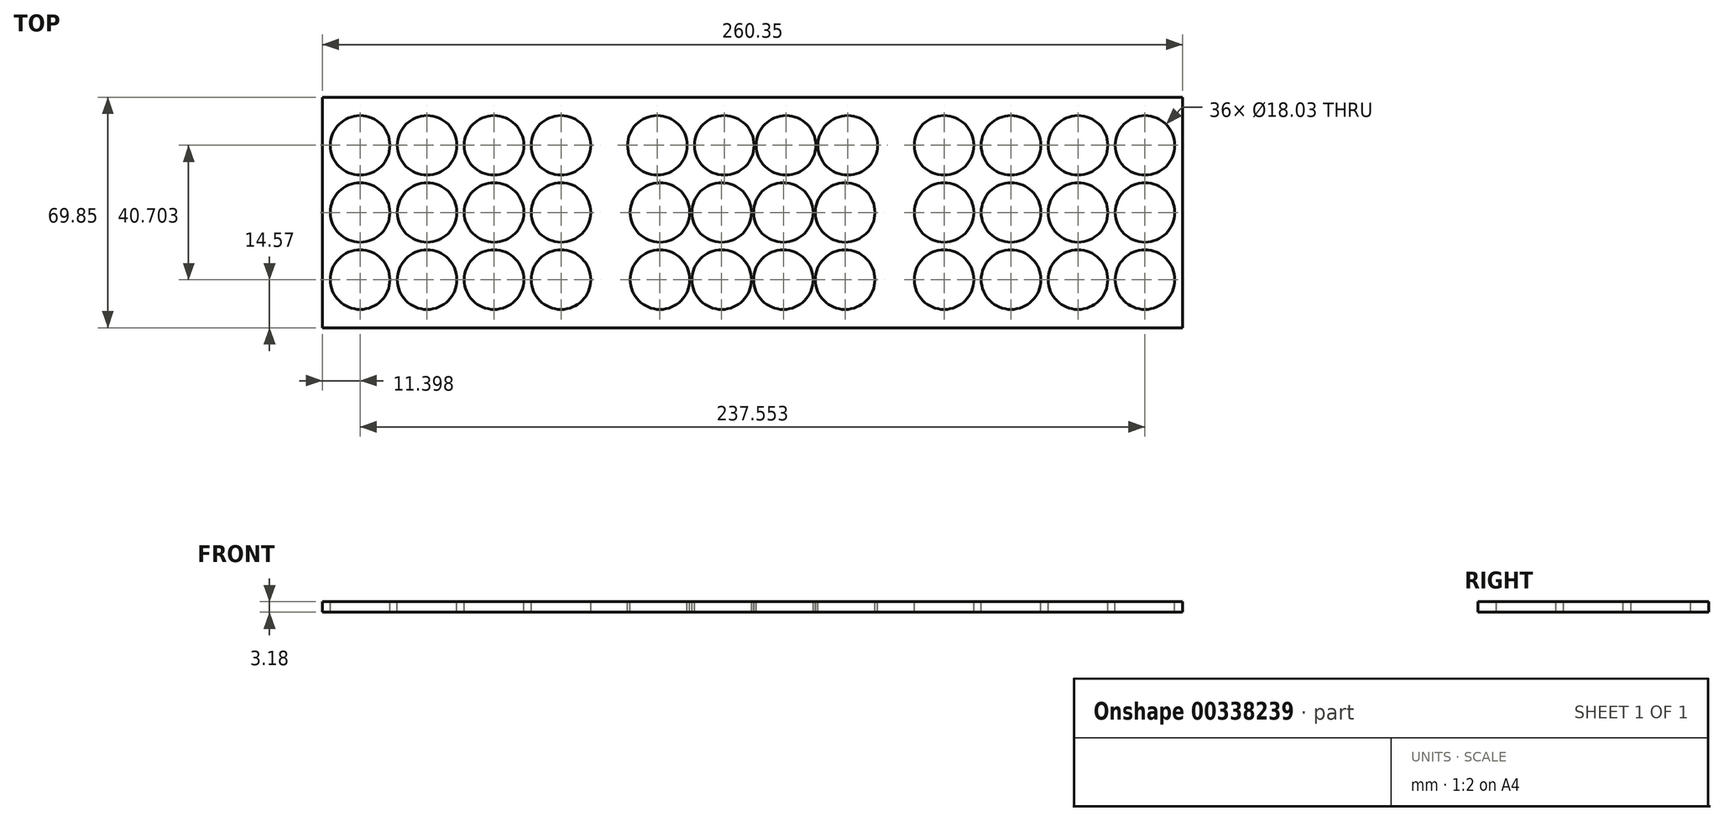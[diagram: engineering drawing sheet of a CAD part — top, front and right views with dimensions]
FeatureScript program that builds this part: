
annotation { "Feature Type Name" : "Feature", "Feature Type Description" : "" }
export const myFeature = defineFeature(function(context is Context, id is Id, definition is map)
    precondition{}
    {
        {
            var Q0;
            Q0=qCreatedBy(makeId("Top.planeOp"),FACE);
            var sketch = newSketch(context, id + "F0", { "sketchPlane" : qUnion([Q0])});
            skLineSegment(sketch, "E0.bottom", {"start": v(0, 0) * mm, "end": v(260.35, 0) * mm});
            skLineSegment(sketch, "E0.top", {"start": v(0, 68.26) * mm, "end": v(260.35, 68.26) * mm});
            skLineSegment(sketch, "E0.left", {"start": v(0, 0) * mm, "end": v(0, 68.26) * mm});
            skLineSegment(sketch, "E0.right", {"start": v(260.35, 0) * mm, "end": v(260.35, 68.26) * mm});
            skSolve(sketch);
        }
        {
            var Q0;
            Q0=qSketchRegion(id+"F0",true);
            extrude(context, id + "F1", {"entities" : qUnion([Q0]), "depth" : 3.17 * mm});
        }
        {
            var Q0;
            Q0=makeQuery(id+"F1.opExtrude","CAP_FACE",FACE,{"disambiguationData":[OSD([sQuery(id+"F0.wireOp",EDGE,"E0.bottom"),sQuery(id+"F0.wireOp",EDGE,"E0.top"),sQuery(id+"F0.wireOp",EDGE,"E0.left"),sQuery(id+"F0.wireOp",EDGE,"E0.right")])],"isStart":false});
            var sketch = newSketch(context, id + "F2", { "sketchPlane" : qUnion([Q0])});
            skLineSegment(sketch, "E1.bottom", {"start": v(0, 0) * mm, "end": v(6.35, 0) * mm});
            skLineSegment(sketch, "E1.top", {"start": v(0, 2.38) * mm, "end": v(6.35, 2.38) * mm});
            skLineSegment(sketch, "E1.left", {"start": v(0, 0) * mm, "end": v(0, 2.38) * mm});
            skLineSegment(sketch, "E1.right", {"start": v(6.35, 0) * mm, "end": v(6.35, 2.38) * mm});
            skLineSegment(sketch, "E2", {"start": v(-2.38, 34.13) * mm, "end": v(0, 34.13) * mm, "construction": true});
            skLineSegment(sketch, "E3.MirrorCS", {"start": v(6.35, 68.26) * mm, "end": v(6.35, 65.88) * mm});
            skLineSegment(sketch, "E4.MirrorCS", {"start": v(0, 65.88) * mm, "end": v(6.35, 65.88) * mm});
            skLineSegment(sketch, "E5.MirrorCS", {"start": v(0, 68.26) * mm, "end": v(6.35, 68.26) * mm});
            skLineSegment(sketch, "E6.MirrorCS", {"start": v(0, 68.26) * mm, "end": v(0, 65.88) * mm});
            skCircle(sketch, "E7", {"center": v(11.4, 54.48) * mm, "radius": 9.02 * mm});
            skLineSegment(sketch, "E8", {"start": v(11.4, 54.48) * mm, "end": v(31.67, 54.48) * mm, "construction": true});
            skCircle(sketch, "E9", {"center": v(31.67, 54.48) * mm, "radius": 9.02 * mm});
            skLineSegment(sketch, "E10.1.0.0", {"start": v(31.67, 54.48) * mm, "end": v(51.94, 54.48) * mm, "construction": true});
            skCircle(sketch, "E10.1.0.1", {"center": v(51.94, 54.48) * mm, "radius": 9.02 * mm});
            skCircle(sketch, "E10.2.0.1", {"center": v(72.21, 54.48) * mm, "radius": 9.02 * mm});
            skLineSegment(sketch, "E11", {"start": v(0, 68.26) * mm, "end": v(0, 155.05) * mm, "construction": true});
            skLineSegment(sketch, "E12", {"start": v(0, 155.05) * mm, "end": v(86.78, 155.05) * mm, "construction": true});
            skLineSegment(sketch, "E13", {"start": v(86.78, 155.05) * mm, "end": v(173.57, 155.05) * mm, "construction": true});
            skLineSegment(sketch, "E14", {"start": v(173.57, 155.05) * mm, "end": v(260.35, 155.05) * mm, "construction": true});
            skLineSegment(sketch, "E15", {"start": v(260.35, 155.05) * mm, "end": v(260.35, 68.26) * mm, "construction": true});
            skLineSegment(sketch, "E16", {"start": v(86.78, 155.05) * mm, "end": v(86.78, 54.48) * mm, "construction": true});
            skLineSegment(sketch, "E17", {"start": v(0, 34.13) * mm, "end": v(2.38, 34.13) * mm, "construction": true});
            skCircle(sketch, "E18", {"center": v(101.36, 54.48) * mm, "radius": 9.02 * mm});
            skLineSegment(sketch, "E19", {"start": v(72.21, 54.48) * mm, "end": v(81.23, 54.48) * mm, "construction": true});
            skLineSegment(sketch, "E20", {"start": v(81.23, 54.48) * mm, "end": v(92.34, 54.48) * mm, "construction": true});
            skLineSegment(sketch, "E21", {"start": v(92.34, 54.48) * mm, "end": v(101.36, 54.48) * mm, "construction": true});
            skLineSegment(sketch, "E22", {"start": v(72.21, 54.48) * mm, "end": v(63.2, 54.48) * mm, "construction": true});
            skLineSegment(sketch, "E23", {"start": v(63.2, 54.48) * mm, "end": v(60.96, 54.48) * mm, "construction": true});
            skLineSegment(sketch, "E24", {"start": v(60.96, 54.48) * mm, "end": v(51.94, 54.48) * mm, "construction": true});
            skLineSegment(sketch, "E25", {"start": v(11.4, 54.48) * mm, "end": v(11.4, 63.5) * mm, "construction": true});
            skLineSegment(sketch, "E26", {"start": v(11.4, 54.48) * mm, "end": v(2.38, 54.48) * mm, "construction": true});
            skLineSegment(sketch, "E27", {"start": v(2.38, 54.48) * mm, "end": v(0, 54.48) * mm, "construction": true});
            skLineSegment(sketch, "E28", {"start": v(51.94, 54.48) * mm, "end": v(51.94, 34.21) * mm, "construction": true});
            skLineSegment(sketch, "E29", {"start": v(51.94, 34.21) * mm, "end": v(72.21, 34.21) * mm, "construction": true});
            skLineSegment(sketch, "E30", {"start": v(72.21, 34.21) * mm, "end": v(72.21, 54.48) * mm, "construction": true});
            skLineSegment(sketch, "E31", {"start": v(2.38, 34.13) * mm, "end": v(11.4, 34.13) * mm, "construction": true});
            skLineSegment(sketch, "E32", {"start": v(173.57, 155.05) * mm, "end": v(173.57, 54.48) * mm});
            skLineSegment(sketch, "E33", {"start": v(168.01, 54.48) * mm, "end": v(179.12, 54.48) * mm, "construction": true});
            skLineSegment(sketch, "E34", {"start": v(101.36, 54.48) * mm, "end": v(121.63, 54.48) * mm, "construction": true});
            skCircle(sketch, "E35", {"center": v(121.63, 54.48) * mm, "radius": 9.02 * mm});
            skCircle(sketch, "E36.1.0.0", {"center": v(140.31, 54.48) * mm, "radius": 9.02 * mm});
            skLineSegment(sketch, "E36.1.0.1", {"start": v(121.63, 54.48) * mm, "end": v(140.31, 54.48) * mm, "construction": true});
            skCircle(sketch, "E36.2.0.0", {"center": v(159, 54.48) * mm, "radius": 9.02 * mm});
            skLineSegment(sketch, "E36.2.0.1", {"start": v(140.31, 54.48) * mm, "end": v(159, 54.48) * mm, "construction": true});
            skLineSegment(sketch, "E37", {"start": v(159, 54.48) * mm, "end": v(168.01, 54.48) * mm, "construction": true});
            skLineSegment(sketch, "E38", {"start": v(179.12, 54.48) * mm, "end": v(188.14, 54.48) * mm, "construction": true});
            skCircle(sketch, "E39", {"center": v(188.14, 54.48) * mm, "radius": 9.02 * mm});
            skLineSegment(sketch, "E40", {"start": v(188.14, 54.48) * mm, "end": v(208.41, 54.48) * mm, "construction": true});
            skLineSegment(sketch, "E41", {"start": v(208.41, 54.48) * mm, "end": v(228.68, 54.48) * mm, "construction": true});
            skLineSegment(sketch, "E42", {"start": v(228.68, 54.48) * mm, "end": v(248.95, 54.48) * mm, "construction": true});
            skCircle(sketch, "E43", {"center": v(208.41, 54.48) * mm, "radius": 9.02 * mm});
            skCircle(sketch, "E44", {"center": v(228.68, 54.48) * mm, "radius": 9.02 * mm});
            skCircle(sketch, "E45", {"center": v(248.95, 54.48) * mm, "radius": 9.02 * mm});
            skCircle(sketch, "E46", {"center": v(11.4, 34.13) * mm, "radius": 9.02 * mm});
            skLineSegment(sketch, "E47", {"start": v(11.4, 34.13) * mm, "end": v(31.67, 34.13) * mm, "construction": true});
            skLineSegment(sketch, "E48", {"start": v(31.67, 34.13) * mm, "end": v(51.94, 34.13) * mm, "construction": true});
            skLineSegment(sketch, "E49", {"start": v(51.94, 34.13) * mm, "end": v(72.21, 34.13) * mm, "construction": true});
            skCircle(sketch, "E50", {"center": v(31.67, 34.13) * mm, "radius": 9.02 * mm});
            skCircle(sketch, "E51", {"center": v(51.94, 34.13) * mm, "radius": 9.02 * mm});
            skCircle(sketch, "E52", {"center": v(72.21, 34.13) * mm, "radius": 9.02 * mm});
            skLineSegment(sketch, "E53", {"start": v(260.35, 34.13) * mm, "end": v(257.97, 34.13) * mm, "construction": true});
            skLineSegment(sketch, "E54", {"start": v(257.97, 34.13) * mm, "end": v(248.95, 34.13) * mm, "construction": true});
            skCircle(sketch, "E55", {"center": v(248.95, 34.13) * mm, "radius": 9.02 * mm});
            skLineSegment(sketch, "E56", {"start": v(248.95, 34.13) * mm, "end": v(228.68, 34.13) * mm, "construction": true});
            skLineSegment(sketch, "E57", {"start": v(228.68, 34.13) * mm, "end": v(208.41, 34.13) * mm, "construction": true});
            skLineSegment(sketch, "E58", {"start": v(208.41, 34.13) * mm, "end": v(188.14, 34.13) * mm, "construction": true});
            skCircle(sketch, "E59", {"center": v(228.68, 34.13) * mm, "radius": 9.02 * mm});
            skCircle(sketch, "E60", {"center": v(208.41, 34.13) * mm, "radius": 9.02 * mm});
            skCircle(sketch, "E61", {"center": v(188.14, 34.13) * mm, "radius": 9.02 * mm});
            skLineSegment(sketch, "E62", {"start": v(72.21, 34.13) * mm, "end": v(102.15, 34.13) * mm, "construction": true});
            skLineSegment(sketch, "E63", {"start": v(102.15, 34.13) * mm, "end": v(120.83, 34.13) * mm, "construction": true});
            skLineSegment(sketch, "E64", {"start": v(120.83, 34.13) * mm, "end": v(139.52, 34.13) * mm, "construction": true});
            skLineSegment(sketch, "E65", {"start": v(139.52, 34.13) * mm, "end": v(158.2, 34.13) * mm, "construction": true});
            skCircle(sketch, "E66", {"center": v(102.15, 34.13) * mm, "radius": 9.02 * mm});
            skCircle(sketch, "E67", {"center": v(120.83, 34.13) * mm, "radius": 9.02 * mm});
            skCircle(sketch, "E68", {"center": v(139.52, 34.13) * mm, "radius": 9.02 * mm});
            skCircle(sketch, "E69", {"center": v(158.2, 34.13) * mm, "radius": 9.02 * mm});
            skLineSegment(sketch, "E70", {"start": v(158.2, 34.13) * mm, "end": v(188.14, 34.13) * mm, "construction": true});
            skLineSegment(sketch, "E71", {"start": v(0, 13.78) * mm, "end": v(2.38, 13.78) * mm, "construction": true});
            skLineSegment(sketch, "E72", {"start": v(2.38, 13.78) * mm, "end": v(11.4, 13.78) * mm, "construction": true});
            skCircle(sketch, "E73", {"center": v(11.4, 13.78) * mm, "radius": 9.02 * mm});
            skLineSegment(sketch, "E74", {"start": v(11.4, 13.78) * mm, "end": v(11.4, 4.76) * mm, "construction": true});
            skLineSegment(sketch, "E75", {"start": v(11.4, 4.76) * mm, "end": v(11.4, 2.38) * mm, "construction": true});
            skLineSegment(sketch, "E76", {"start": v(260.35, 13.78) * mm, "end": v(257.97, 13.78) * mm, "construction": true});
            skLineSegment(sketch, "E77", {"start": v(257.97, 13.78) * mm, "end": v(248.95, 13.78) * mm, "construction": true});
            skLineSegment(sketch, "E78", {"start": v(248.95, 13.78) * mm, "end": v(248.95, 4.76) * mm, "construction": true});
            skLineSegment(sketch, "E79", {"start": v(248.95, 4.76) * mm, "end": v(248.95, 2.38) * mm, "construction": true});
            skCircle(sketch, "E80", {"center": v(248.95, 13.78) * mm, "radius": 9.02 * mm});
            skLineSegment(sketch, "E81", {"start": v(248.95, 13.78) * mm, "end": v(228.68, 13.78) * mm, "construction": true});
            skLineSegment(sketch, "E82", {"start": v(228.68, 13.78) * mm, "end": v(208.41, 13.78) * mm, "construction": true});
            skLineSegment(sketch, "E83", {"start": v(208.41, 13.78) * mm, "end": v(188.14, 13.78) * mm, "construction": true});
            skCircle(sketch, "E84", {"center": v(228.68, 13.78) * mm, "radius": 9.02 * mm});
            skCircle(sketch, "E85", {"center": v(208.41, 13.78) * mm, "radius": 9.02 * mm});
            skCircle(sketch, "E86", {"center": v(188.14, 13.78) * mm, "radius": 9.02 * mm});
            skLineSegment(sketch, "E87", {"start": v(11.4, 13.78) * mm, "end": v(31.67, 13.78) * mm, "construction": true});
            skLineSegment(sketch, "E88", {"start": v(31.67, 13.78) * mm, "end": v(51.94, 13.78) * mm, "construction": true});
            skLineSegment(sketch, "E89", {"start": v(51.94, 13.78) * mm, "end": v(72.21, 13.78) * mm, "construction": true});
            skCircle(sketch, "E90", {"center": v(31.67, 13.78) * mm, "radius": 9.02 * mm});
            skCircle(sketch, "E91", {"center": v(51.94, 13.78) * mm, "radius": 9.02 * mm});
            skCircle(sketch, "E92", {"center": v(72.21, 13.78) * mm, "radius": 9.02 * mm});
            skLineSegment(sketch, "E93", {"start": v(102.15, 13.78) * mm, "end": v(120.83, 13.78) * mm, "construction": true});
            skLineSegment(sketch, "E94", {"start": v(120.83, 13.78) * mm, "end": v(139.52, 13.78) * mm, "construction": true});
            skLineSegment(sketch, "E95", {"start": v(139.52, 13.78) * mm, "end": v(158.2, 13.78) * mm, "construction": true});
            skCircle(sketch, "E96", {"center": v(102.15, 13.78) * mm, "radius": 9.02 * mm});
            skCircle(sketch, "E97", {"center": v(120.83, 13.78) * mm, "radius": 9.02 * mm});
            skCircle(sketch, "E98", {"center": v(139.52, 13.78) * mm, "radius": 9.02 * mm});
            skCircle(sketch, "E99", {"center": v(158.2, 13.78) * mm, "radius": 9.02 * mm});
            skLineSegment(sketch, "E100", {"start": v(72.21, 13.78) * mm, "end": v(102.15, 13.78) * mm, "construction": true});
            skLineSegment(sketch, "E101", {"start": v(188.14, 13.78) * mm, "end": v(158.2, 13.78) * mm, "construction": true});
            skLineSegment(sketch, "E102", {"start": v(6.35, 65.88) * mm, "end": v(12.7, 65.88) * mm, "construction": true});
            skLineSegment(sketch, "E103.bottom", {"start": v(12.7, 65.88) * mm, "end": v(19.05, 65.88) * mm});
            skLineSegment(sketch, "E103.top", {"start": v(12.7, 68.26) * mm, "end": v(19.05, 68.26) * mm});
            skLineSegment(sketch, "E103.left", {"start": v(12.7, 65.88) * mm, "end": v(12.7, 68.26) * mm});
            skLineSegment(sketch, "E103.right", {"start": v(19.05, 65.88) * mm, "end": v(19.05, 68.26) * mm});
            skLineSegment(sketch, "E104", {"start": v(6.35, 2.38) * mm, "end": v(12.7, 2.38) * mm, "construction": true});
            skLineSegment(sketch, "E105.bottom", {"start": v(12.7, 2.38) * mm, "end": v(19.05, 2.38) * mm});
            skLineSegment(sketch, "E105.top", {"start": v(12.7, 0) * mm, "end": v(19.05, 0) * mm});
            skLineSegment(sketch, "E105.left", {"start": v(12.7, 2.38) * mm, "end": v(12.7, 0) * mm});
            skLineSegment(sketch, "E105.right", {"start": v(19.05, 2.38) * mm, "end": v(19.05, 0) * mm});
            skLineSegment(sketch, "E106.1.0.0", {"start": v(25.4, 2.38) * mm, "end": v(31.75, 2.38) * mm});
            skLineSegment(sketch, "E106.1.0.1", {"start": v(25.4, 0) * mm, "end": v(31.75, 0) * mm});
            skLineSegment(sketch, "E106.1.0.2", {"start": v(19.05, 2.38) * mm, "end": v(25.4, 2.38) * mm, "construction": true});
            skLineSegment(sketch, "E106.1.0.3", {"start": v(25.4, 2.38) * mm, "end": v(25.4, 0) * mm});
            skLineSegment(sketch, "E106.1.0.4", {"start": v(31.75, 2.38) * mm, "end": v(31.75, 0) * mm});
            skLineSegment(sketch, "E106.2.0.0", {"start": v(38.1, 2.38) * mm, "end": v(44.45, 2.38) * mm});
            skLineSegment(sketch, "E106.2.0.1", {"start": v(38.1, 0) * mm, "end": v(44.45, 0) * mm});
            skLineSegment(sketch, "E106.2.0.2", {"start": v(31.75, 2.38) * mm, "end": v(38.1, 2.38) * mm, "construction": true});
            skLineSegment(sketch, "E106.2.0.3", {"start": v(38.1, 2.38) * mm, "end": v(38.1, 0) * mm});
            skLineSegment(sketch, "E106.2.0.4", {"start": v(44.45, 2.38) * mm, "end": v(44.45, 0) * mm});
            skLineSegment(sketch, "E106.direction1", {"start": v(6.35, 2.38) * mm, "end": v(19.05, 2.38) * mm, "construction": true});
            skLineSegment(sketch, "E107.0.3.0", {"start": v(50.8, 2.38) * mm, "end": v(57.15, 2.38) * mm});
            skLineSegment(sketch, "E107.3.3.0", {"start": v(50.8, 0) * mm, "end": v(57.15, 0) * mm});
            skLineSegment(sketch, "E107.6.3.0", {"start": v(44.45, 2.38) * mm, "end": v(50.8, 2.38) * mm, "construction": true});
            skLineSegment(sketch, "E107.9.3.0", {"start": v(50.8, 2.38) * mm, "end": v(50.8, 0) * mm});
            skLineSegment(sketch, "E107.12.3.0", {"start": v(57.15, 2.38) * mm, "end": v(57.15, 0) * mm});
            skLineSegment(sketch, "E107.0.4.0", {"start": v(63.5, 2.38) * mm, "end": v(69.85, 2.38) * mm});
            skLineSegment(sketch, "E107.3.4.0", {"start": v(63.5, 0) * mm, "end": v(69.85, 0) * mm});
            skLineSegment(sketch, "E107.6.4.0", {"start": v(57.15, 2.38) * mm, "end": v(63.5, 2.38) * mm, "construction": true});
            skLineSegment(sketch, "E107.9.4.0", {"start": v(63.5, 2.38) * mm, "end": v(63.5, 0) * mm});
            skLineSegment(sketch, "E107.12.4.0", {"start": v(69.85, 2.38) * mm, "end": v(69.85, 0) * mm});
            skLineSegment(sketch, "E107.0.5.0", {"start": v(76.2, 2.38) * mm, "end": v(82.55, 2.38) * mm});
            skLineSegment(sketch, "E107.3.5.0", {"start": v(76.2, 0) * mm, "end": v(82.55, 0) * mm});
            skLineSegment(sketch, "E107.6.5.0", {"start": v(69.85, 2.38) * mm, "end": v(76.2, 2.38) * mm, "construction": true});
            skLineSegment(sketch, "E107.9.5.0", {"start": v(76.2, 2.38) * mm, "end": v(76.2, 0) * mm});
            skLineSegment(sketch, "E107.12.5.0", {"start": v(82.55, 2.38) * mm, "end": v(82.55, 0) * mm});
            skLineSegment(sketch, "E107.0.6.0", {"start": v(88.9, 2.38) * mm, "end": v(95.25, 2.38) * mm});
            skLineSegment(sketch, "E107.3.6.0", {"start": v(88.9, 0) * mm, "end": v(95.25, 0) * mm});
            skLineSegment(sketch, "E107.6.6.0", {"start": v(82.55, 2.38) * mm, "end": v(88.9, 2.38) * mm, "construction": true});
            skLineSegment(sketch, "E107.9.6.0", {"start": v(88.9, 2.38) * mm, "end": v(88.9, 0) * mm});
            skLineSegment(sketch, "E107.12.6.0", {"start": v(95.25, 2.38) * mm, "end": v(95.25, 0) * mm});
            skLineSegment(sketch, "E107.0.7.0", {"start": v(101.6, 2.38) * mm, "end": v(107.95, 2.38) * mm});
            skLineSegment(sketch, "E107.3.7.0", {"start": v(101.6, 0) * mm, "end": v(107.95, 0) * mm});
            skLineSegment(sketch, "E107.6.7.0", {"start": v(95.25, 2.38) * mm, "end": v(101.6, 2.38) * mm, "construction": true});
            skLineSegment(sketch, "E107.9.7.0", {"start": v(101.6, 2.38) * mm, "end": v(101.6, 0) * mm});
            skLineSegment(sketch, "E107.12.7.0", {"start": v(107.95, 2.38) * mm, "end": v(107.95, 0) * mm});
            skLineSegment(sketch, "E107.0.8.0", {"start": v(114.3, 2.38) * mm, "end": v(120.65, 2.38) * mm});
            skLineSegment(sketch, "E107.3.8.0", {"start": v(114.3, 0) * mm, "end": v(120.65, 0) * mm});
            skLineSegment(sketch, "E107.6.8.0", {"start": v(107.95, 2.38) * mm, "end": v(114.3, 2.38) * mm, "construction": true});
            skLineSegment(sketch, "E107.9.8.0", {"start": v(114.3, 2.38) * mm, "end": v(114.3, 0) * mm});
            skLineSegment(sketch, "E107.12.8.0", {"start": v(120.65, 2.38) * mm, "end": v(120.65, 0) * mm});
            skLineSegment(sketch, "E107.0.9.0", {"start": v(127, 2.38) * mm, "end": v(133.35, 2.38) * mm});
            skLineSegment(sketch, "E107.3.9.0", {"start": v(127, 0) * mm, "end": v(133.35, 0) * mm});
            skLineSegment(sketch, "E107.6.9.0", {"start": v(120.65, 2.38) * mm, "end": v(127, 2.38) * mm, "construction": true});
            skLineSegment(sketch, "E107.9.9.0", {"start": v(127, 2.38) * mm, "end": v(127, 0) * mm});
            skLineSegment(sketch, "E107.12.9.0", {"start": v(133.35, 2.38) * mm, "end": v(133.35, 0) * mm});
            skLineSegment(sketch, "E107.0.10.0", {"start": v(139.7, 2.38) * mm, "end": v(146.05, 2.38) * mm});
            skLineSegment(sketch, "E107.3.10.0", {"start": v(139.7, 0) * mm, "end": v(146.05, 0) * mm});
            skLineSegment(sketch, "E107.6.10.0", {"start": v(133.35, 2.38) * mm, "end": v(139.7, 2.38) * mm, "construction": true});
            skLineSegment(sketch, "E107.9.10.0", {"start": v(139.7, 2.38) * mm, "end": v(139.7, 0) * mm});
            skLineSegment(sketch, "E107.12.10.0", {"start": v(146.05, 2.38) * mm, "end": v(146.05, 0) * mm});
            skLineSegment(sketch, "E107.0.11.0", {"start": v(152.4, 2.38) * mm, "end": v(158.75, 2.38) * mm});
            skLineSegment(sketch, "E107.3.11.0", {"start": v(152.4, 0) * mm, "end": v(158.75, 0) * mm});
            skLineSegment(sketch, "E107.6.11.0", {"start": v(146.05, 2.38) * mm, "end": v(152.4, 2.38) * mm, "construction": true});
            skLineSegment(sketch, "E107.9.11.0", {"start": v(152.4, 2.38) * mm, "end": v(152.4, 0) * mm});
            skLineSegment(sketch, "E107.12.11.0", {"start": v(158.75, 2.38) * mm, "end": v(158.75, 0) * mm});
            skLineSegment(sketch, "E107.0.12.0", {"start": v(165.1, 2.38) * mm, "end": v(171.45, 2.38) * mm});
            skLineSegment(sketch, "E107.3.12.0", {"start": v(165.1, 0) * mm, "end": v(171.45, 0) * mm});
            skLineSegment(sketch, "E107.6.12.0", {"start": v(158.75, 2.38) * mm, "end": v(165.1, 2.38) * mm, "construction": true});
            skLineSegment(sketch, "E107.9.12.0", {"start": v(165.1, 2.38) * mm, "end": v(165.1, 0) * mm});
            skLineSegment(sketch, "E107.12.12.0", {"start": v(171.45, 2.38) * mm, "end": v(171.45, 0) * mm});
            skLineSegment(sketch, "E107.0.13.0", {"start": v(177.8, 2.38) * mm, "end": v(184.15, 2.38) * mm});
            skLineSegment(sketch, "E107.3.13.0", {"start": v(177.8, 0) * mm, "end": v(184.15, 0) * mm});
            skLineSegment(sketch, "E107.6.13.0", {"start": v(171.45, 2.38) * mm, "end": v(177.8, 2.38) * mm, "construction": true});
            skLineSegment(sketch, "E107.9.13.0", {"start": v(177.8, 2.38) * mm, "end": v(177.8, 0) * mm});
            skLineSegment(sketch, "E107.12.13.0", {"start": v(184.15, 2.38) * mm, "end": v(184.15, 0) * mm});
            skLineSegment(sketch, "E107.0.14.0", {"start": v(190.5, 2.38) * mm, "end": v(196.85, 2.38) * mm});
            skLineSegment(sketch, "E107.3.14.0", {"start": v(190.5, 0) * mm, "end": v(196.85, 0) * mm});
            skLineSegment(sketch, "E107.6.14.0", {"start": v(184.15, 2.38) * mm, "end": v(190.5, 2.38) * mm, "construction": true});
            skLineSegment(sketch, "E107.9.14.0", {"start": v(190.5, 2.38) * mm, "end": v(190.5, 0) * mm});
            skLineSegment(sketch, "E107.12.14.0", {"start": v(196.85, 2.38) * mm, "end": v(196.85, 0) * mm});
            skLineSegment(sketch, "E107.0.15.0", {"start": v(203.2, 2.38) * mm, "end": v(209.55, 2.38) * mm});
            skLineSegment(sketch, "E107.3.15.0", {"start": v(203.2, 0) * mm, "end": v(209.55, 0) * mm});
            skLineSegment(sketch, "E107.6.15.0", {"start": v(196.85, 2.38) * mm, "end": v(203.2, 2.38) * mm, "construction": true});
            skLineSegment(sketch, "E107.9.15.0", {"start": v(203.2, 2.38) * mm, "end": v(203.2, 0) * mm});
            skLineSegment(sketch, "E107.12.15.0", {"start": v(209.55, 2.38) * mm, "end": v(209.55, 0) * mm});
            skLineSegment(sketch, "E107.0.16.0", {"start": v(215.9, 2.38) * mm, "end": v(222.25, 2.38) * mm});
            skLineSegment(sketch, "E107.3.16.0", {"start": v(215.9, 0) * mm, "end": v(222.25, 0) * mm});
            skLineSegment(sketch, "E107.6.16.0", {"start": v(209.55, 2.38) * mm, "end": v(215.9, 2.38) * mm, "construction": true});
            skLineSegment(sketch, "E107.9.16.0", {"start": v(215.9, 2.38) * mm, "end": v(215.9, 0) * mm});
            skLineSegment(sketch, "E107.12.16.0", {"start": v(222.25, 2.38) * mm, "end": v(222.25, 0) * mm});
            skLineSegment(sketch, "E107.0.17.0", {"start": v(228.6, 2.38) * mm, "end": v(234.95, 2.38) * mm});
            skLineSegment(sketch, "E107.3.17.0", {"start": v(228.6, 0) * mm, "end": v(234.95, 0) * mm});
            skLineSegment(sketch, "E107.6.17.0", {"start": v(222.25, 2.38) * mm, "end": v(228.6, 2.38) * mm, "construction": true});
            skLineSegment(sketch, "E107.9.17.0", {"start": v(228.6, 2.38) * mm, "end": v(228.6, 0) * mm});
            skLineSegment(sketch, "E107.12.17.0", {"start": v(234.95, 2.38) * mm, "end": v(234.95, 0) * mm});
            skLineSegment(sketch, "E107.0.18.0", {"start": v(241.3, 2.38) * mm, "end": v(247.65, 2.38) * mm});
            skLineSegment(sketch, "E107.3.18.0", {"start": v(241.3, 0) * mm, "end": v(247.65, 0) * mm});
            skLineSegment(sketch, "E107.6.18.0", {"start": v(234.95, 2.38) * mm, "end": v(241.3, 2.38) * mm, "construction": true});
            skLineSegment(sketch, "E107.9.18.0", {"start": v(241.3, 2.38) * mm, "end": v(241.3, 0) * mm});
            skLineSegment(sketch, "E107.12.18.0", {"start": v(247.65, 2.38) * mm, "end": v(247.65, 0) * mm});
            skLineSegment(sketch, "E107.0.19.0", {"start": v(254, 2.38) * mm, "end": v(260.35, 2.38) * mm});
            skLineSegment(sketch, "E107.3.19.0", {"start": v(254, 0) * mm, "end": v(260.35, 0) * mm});
            skLineSegment(sketch, "E107.6.19.0", {"start": v(247.65, 2.38) * mm, "end": v(254, 2.38) * mm, "construction": true});
            skLineSegment(sketch, "E107.9.19.0", {"start": v(254, 2.38) * mm, "end": v(254, 0) * mm});
            skLineSegment(sketch, "E107.12.19.0", {"start": v(260.35, 2.38) * mm, "end": v(260.35, 0) * mm});
            skLineSegment(sketch, "E107.0.20.0", {"start": v(266.7, 2.38) * mm, "end": v(273.05, 2.38) * mm});
            skLineSegment(sketch, "E107.3.20.0", {"start": v(266.7, 0) * mm, "end": v(273.05, 0) * mm});
            skLineSegment(sketch, "E107.6.20.0", {"start": v(260.35, 2.38) * mm, "end": v(266.7, 2.38) * mm, "construction": true});
            skLineSegment(sketch, "E107.9.20.0", {"start": v(266.7, 2.38) * mm, "end": v(266.7, 0) * mm});
            skLineSegment(sketch, "E107.12.20.0", {"start": v(273.05, 2.38) * mm, "end": v(273.05, 0) * mm});
            skLineSegment(sketch, "E107.0.21.0", {"start": v(279.4, 2.38) * mm, "end": v(285.75, 2.38) * mm});
            skLineSegment(sketch, "E107.3.21.0", {"start": v(279.4, 0) * mm, "end": v(285.75, 0) * mm});
            skLineSegment(sketch, "E107.6.21.0", {"start": v(273.05, 2.38) * mm, "end": v(279.4, 2.38) * mm, "construction": true});
            skLineSegment(sketch, "E107.9.21.0", {"start": v(279.4, 2.38) * mm, "end": v(279.4, 0) * mm});
            skLineSegment(sketch, "E107.12.21.0", {"start": v(285.75, 2.38) * mm, "end": v(285.75, 0) * mm});
            skLineSegment(sketch, "E108.1.0.0", {"start": v(25.4, 65.88) * mm, "end": v(31.75, 65.88) * mm});
            skLineSegment(sketch, "E108.1.0.1", {"start": v(25.4, 65.88) * mm, "end": v(25.4, 68.26) * mm});
            skLineSegment(sketch, "E108.1.0.2", {"start": v(25.4, 68.26) * mm, "end": v(31.75, 68.26) * mm});
            skLineSegment(sketch, "E108.1.0.3", {"start": v(31.75, 65.88) * mm, "end": v(31.75, 68.26) * mm});
            skLineSegment(sketch, "E108.1.0.4", {"start": v(19.05, 65.88) * mm, "end": v(25.4, 65.88) * mm, "construction": true});
            skLineSegment(sketch, "E108.2.0.0", {"start": v(38.1, 65.88) * mm, "end": v(44.45, 65.88) * mm});
            skLineSegment(sketch, "E108.2.0.1", {"start": v(38.1, 65.88) * mm, "end": v(38.1, 68.26) * mm});
            skLineSegment(sketch, "E108.2.0.2", {"start": v(38.1, 68.26) * mm, "end": v(44.45, 68.26) * mm});
            skLineSegment(sketch, "E108.2.0.3", {"start": v(44.45, 65.88) * mm, "end": v(44.45, 68.26) * mm});
            skLineSegment(sketch, "E108.2.0.4", {"start": v(31.75, 65.88) * mm, "end": v(38.1, 65.88) * mm, "construction": true});
            skLineSegment(sketch, "E108.3.0.0", {"start": v(50.8, 65.88) * mm, "end": v(57.15, 65.88) * mm});
            skLineSegment(sketch, "E108.3.0.1", {"start": v(50.8, 65.88) * mm, "end": v(50.8, 68.26) * mm});
            skLineSegment(sketch, "E108.3.0.2", {"start": v(50.8, 68.26) * mm, "end": v(57.15, 68.26) * mm});
            skLineSegment(sketch, "E108.3.0.3", {"start": v(57.15, 65.88) * mm, "end": v(57.15, 68.26) * mm});
            skLineSegment(sketch, "E108.3.0.4", {"start": v(44.45, 65.88) * mm, "end": v(50.8, 65.88) * mm, "construction": true});
            skLineSegment(sketch, "E108.4.0.0", {"start": v(63.5, 65.88) * mm, "end": v(69.85, 65.88) * mm});
            skLineSegment(sketch, "E108.4.0.1", {"start": v(63.5, 65.88) * mm, "end": v(63.5, 68.26) * mm});
            skLineSegment(sketch, "E108.4.0.2", {"start": v(63.5, 68.26) * mm, "end": v(69.85, 68.26) * mm});
            skLineSegment(sketch, "E108.4.0.3", {"start": v(69.85, 65.88) * mm, "end": v(69.85, 68.26) * mm});
            skLineSegment(sketch, "E108.4.0.4", {"start": v(57.15, 65.88) * mm, "end": v(63.5, 65.88) * mm, "construction": true});
            skLineSegment(sketch, "E108.5.0.0", {"start": v(76.2, 65.88) * mm, "end": v(82.55, 65.88) * mm});
            skLineSegment(sketch, "E108.5.0.1", {"start": v(76.2, 65.88) * mm, "end": v(76.2, 68.26) * mm});
            skLineSegment(sketch, "E108.5.0.2", {"start": v(76.2, 68.26) * mm, "end": v(82.55, 68.26) * mm});
            skLineSegment(sketch, "E108.5.0.3", {"start": v(82.55, 65.88) * mm, "end": v(82.55, 68.26) * mm});
            skLineSegment(sketch, "E108.5.0.4", {"start": v(69.85, 65.88) * mm, "end": v(76.2, 65.88) * mm, "construction": true});
            skLineSegment(sketch, "E108.6.0.0", {"start": v(88.9, 65.88) * mm, "end": v(95.25, 65.88) * mm});
            skLineSegment(sketch, "E108.6.0.1", {"start": v(88.9, 65.88) * mm, "end": v(88.9, 68.26) * mm});
            skLineSegment(sketch, "E108.6.0.2", {"start": v(88.9, 68.26) * mm, "end": v(95.25, 68.26) * mm});
            skLineSegment(sketch, "E108.6.0.3", {"start": v(95.25, 65.88) * mm, "end": v(95.25, 68.26) * mm});
            skLineSegment(sketch, "E108.6.0.4", {"start": v(82.55, 65.88) * mm, "end": v(88.9, 65.88) * mm, "construction": true});
            skLineSegment(sketch, "E108.7.0.0", {"start": v(101.6, 65.88) * mm, "end": v(107.95, 65.88) * mm});
            skLineSegment(sketch, "E108.7.0.1", {"start": v(101.6, 65.88) * mm, "end": v(101.6, 68.26) * mm});
            skLineSegment(sketch, "E108.7.0.2", {"start": v(101.6, 68.26) * mm, "end": v(107.95, 68.26) * mm});
            skLineSegment(sketch, "E108.7.0.3", {"start": v(107.95, 65.88) * mm, "end": v(107.95, 68.26) * mm});
            skLineSegment(sketch, "E108.7.0.4", {"start": v(95.25, 65.88) * mm, "end": v(101.6, 65.88) * mm, "construction": true});
            skLineSegment(sketch, "E108.8.0.0", {"start": v(114.3, 65.88) * mm, "end": v(120.65, 65.88) * mm});
            skLineSegment(sketch, "E108.8.0.1", {"start": v(114.3, 65.88) * mm, "end": v(114.3, 68.26) * mm});
            skLineSegment(sketch, "E108.8.0.2", {"start": v(114.3, 68.26) * mm, "end": v(120.65, 68.26) * mm});
            skLineSegment(sketch, "E108.8.0.3", {"start": v(120.65, 65.88) * mm, "end": v(120.65, 68.26) * mm});
            skLineSegment(sketch, "E108.8.0.4", {"start": v(107.95, 65.88) * mm, "end": v(114.3, 65.88) * mm, "construction": true});
            skLineSegment(sketch, "E108.9.0.0", {"start": v(127, 65.88) * mm, "end": v(133.35, 65.88) * mm});
            skLineSegment(sketch, "E108.9.0.1", {"start": v(127, 65.88) * mm, "end": v(127, 68.26) * mm});
            skLineSegment(sketch, "E108.9.0.2", {"start": v(127, 68.26) * mm, "end": v(133.35, 68.26) * mm});
            skLineSegment(sketch, "E108.9.0.3", {"start": v(133.35, 65.88) * mm, "end": v(133.35, 68.26) * mm});
            skLineSegment(sketch, "E108.9.0.4", {"start": v(120.65, 65.88) * mm, "end": v(127, 65.88) * mm, "construction": true});
            skLineSegment(sketch, "E108.10.0.0", {"start": v(139.7, 65.88) * mm, "end": v(146.05, 65.88) * mm});
            skLineSegment(sketch, "E108.10.0.1", {"start": v(139.7, 65.88) * mm, "end": v(139.7, 68.26) * mm});
            skLineSegment(sketch, "E108.10.0.2", {"start": v(139.7, 68.26) * mm, "end": v(146.05, 68.26) * mm});
            skLineSegment(sketch, "E108.10.0.3", {"start": v(146.05, 65.88) * mm, "end": v(146.05, 68.26) * mm});
            skLineSegment(sketch, "E108.10.0.4", {"start": v(133.35, 65.88) * mm, "end": v(139.7, 65.88) * mm, "construction": true});
            skLineSegment(sketch, "E108.11.0.0", {"start": v(152.4, 65.88) * mm, "end": v(158.75, 65.88) * mm});
            skLineSegment(sketch, "E108.11.0.1", {"start": v(152.4, 65.88) * mm, "end": v(152.4, 68.26) * mm});
            skLineSegment(sketch, "E108.11.0.2", {"start": v(152.4, 68.26) * mm, "end": v(158.75, 68.26) * mm});
            skLineSegment(sketch, "E108.11.0.3", {"start": v(158.75, 65.88) * mm, "end": v(158.75, 68.26) * mm});
            skLineSegment(sketch, "E108.11.0.4", {"start": v(146.05, 65.88) * mm, "end": v(152.4, 65.88) * mm, "construction": true});
            skLineSegment(sketch, "E108.12.0.0", {"start": v(165.1, 65.88) * mm, "end": v(171.45, 65.88) * mm});
            skLineSegment(sketch, "E108.12.0.1", {"start": v(165.1, 65.88) * mm, "end": v(165.1, 68.26) * mm});
            skLineSegment(sketch, "E108.12.0.2", {"start": v(165.1, 68.26) * mm, "end": v(171.45, 68.26) * mm});
            skLineSegment(sketch, "E108.12.0.3", {"start": v(171.45, 65.88) * mm, "end": v(171.45, 68.26) * mm});
            skLineSegment(sketch, "E108.12.0.4", {"start": v(158.75, 65.88) * mm, "end": v(165.1, 65.88) * mm, "construction": true});
            skLineSegment(sketch, "E108.13.0.0", {"start": v(177.8, 65.88) * mm, "end": v(184.15, 65.88) * mm});
            skLineSegment(sketch, "E108.13.0.1", {"start": v(177.8, 65.88) * mm, "end": v(177.8, 68.26) * mm});
            skLineSegment(sketch, "E108.13.0.2", {"start": v(177.8, 68.26) * mm, "end": v(184.15, 68.26) * mm});
            skLineSegment(sketch, "E108.13.0.3", {"start": v(184.15, 65.88) * mm, "end": v(184.15, 68.26) * mm});
            skLineSegment(sketch, "E108.13.0.4", {"start": v(171.45, 65.88) * mm, "end": v(177.8, 65.88) * mm, "construction": true});
            skLineSegment(sketch, "E108.14.0.0", {"start": v(190.5, 65.88) * mm, "end": v(196.85, 65.88) * mm});
            skLineSegment(sketch, "E108.14.0.1", {"start": v(190.5, 65.88) * mm, "end": v(190.5, 68.26) * mm});
            skLineSegment(sketch, "E108.14.0.2", {"start": v(190.5, 68.26) * mm, "end": v(196.85, 68.26) * mm});
            skLineSegment(sketch, "E108.14.0.3", {"start": v(196.85, 65.88) * mm, "end": v(196.85, 68.26) * mm});
            skLineSegment(sketch, "E108.14.0.4", {"start": v(184.15, 65.88) * mm, "end": v(190.5, 65.88) * mm, "construction": true});
            skLineSegment(sketch, "E108.15.0.0", {"start": v(203.2, 65.88) * mm, "end": v(209.55, 65.88) * mm});
            skLineSegment(sketch, "E108.15.0.1", {"start": v(203.2, 65.88) * mm, "end": v(203.2, 68.26) * mm});
            skLineSegment(sketch, "E108.15.0.2", {"start": v(203.2, 68.26) * mm, "end": v(209.55, 68.26) * mm});
            skLineSegment(sketch, "E108.15.0.3", {"start": v(209.55, 65.88) * mm, "end": v(209.55, 68.26) * mm});
            skLineSegment(sketch, "E108.15.0.4", {"start": v(196.85, 65.88) * mm, "end": v(203.2, 65.88) * mm, "construction": true});
            skLineSegment(sketch, "E108.16.0.0", {"start": v(215.9, 65.88) * mm, "end": v(222.25, 65.88) * mm});
            skLineSegment(sketch, "E108.16.0.1", {"start": v(215.9, 65.88) * mm, "end": v(215.9, 68.26) * mm});
            skLineSegment(sketch, "E108.16.0.2", {"start": v(215.9, 68.26) * mm, "end": v(222.25, 68.26) * mm});
            skLineSegment(sketch, "E108.16.0.3", {"start": v(222.25, 65.88) * mm, "end": v(222.25, 68.26) * mm});
            skLineSegment(sketch, "E108.16.0.4", {"start": v(209.55, 65.88) * mm, "end": v(215.9, 65.88) * mm, "construction": true});
            skLineSegment(sketch, "E108.17.0.0", {"start": v(228.6, 65.88) * mm, "end": v(234.95, 65.88) * mm});
            skLineSegment(sketch, "E108.17.0.1", {"start": v(228.6, 65.88) * mm, "end": v(228.6, 68.26) * mm});
            skLineSegment(sketch, "E108.17.0.2", {"start": v(228.6, 68.26) * mm, "end": v(234.95, 68.26) * mm});
            skLineSegment(sketch, "E108.17.0.3", {"start": v(234.95, 65.88) * mm, "end": v(234.95, 68.26) * mm});
            skLineSegment(sketch, "E108.17.0.4", {"start": v(222.25, 65.88) * mm, "end": v(228.6, 65.88) * mm, "construction": true});
            skLineSegment(sketch, "E108.18.0.0", {"start": v(241.3, 65.88) * mm, "end": v(247.65, 65.88) * mm});
            skLineSegment(sketch, "E108.18.0.1", {"start": v(241.3, 65.88) * mm, "end": v(241.3, 68.26) * mm});
            skLineSegment(sketch, "E108.18.0.2", {"start": v(241.3, 68.26) * mm, "end": v(247.65, 68.26) * mm});
            skLineSegment(sketch, "E108.18.0.3", {"start": v(247.65, 65.88) * mm, "end": v(247.65, 68.26) * mm});
            skLineSegment(sketch, "E108.18.0.4", {"start": v(234.95, 65.88) * mm, "end": v(241.3, 65.88) * mm, "construction": true});
            skLineSegment(sketch, "E108.19.0.0", {"start": v(254, 65.88) * mm, "end": v(260.35, 65.88) * mm});
            skLineSegment(sketch, "E108.19.0.1", {"start": v(254, 65.88) * mm, "end": v(254, 68.26) * mm});
            skLineSegment(sketch, "E108.19.0.2", {"start": v(254, 68.26) * mm, "end": v(260.35, 68.26) * mm});
            skLineSegment(sketch, "E108.19.0.3", {"start": v(260.35, 65.88) * mm, "end": v(260.35, 68.26) * mm});
            skLineSegment(sketch, "E108.19.0.4", {"start": v(247.65, 65.88) * mm, "end": v(254, 65.88) * mm, "construction": true});
            skLineSegment(sketch, "E108.20.0.0", {"start": v(266.7, 65.88) * mm, "end": v(273.05, 65.88) * mm});
            skLineSegment(sketch, "E108.20.0.1", {"start": v(266.7, 65.88) * mm, "end": v(266.7, 68.26) * mm});
            skLineSegment(sketch, "E108.20.0.2", {"start": v(266.7, 68.26) * mm, "end": v(273.05, 68.26) * mm});
            skLineSegment(sketch, "E108.20.0.3", {"start": v(273.05, 65.88) * mm, "end": v(273.05, 68.26) * mm});
            skLineSegment(sketch, "E108.20.0.4", {"start": v(260.35, 65.88) * mm, "end": v(266.7, 65.88) * mm, "construction": true});
            skLineSegment(sketch, "E108.21.0.0", {"start": v(279.4, 65.88) * mm, "end": v(285.75, 65.88) * mm});
            skLineSegment(sketch, "E108.21.0.1", {"start": v(279.4, 65.88) * mm, "end": v(279.4, 68.26) * mm});
            skLineSegment(sketch, "E108.21.0.2", {"start": v(279.4, 68.26) * mm, "end": v(285.75, 68.26) * mm});
            skLineSegment(sketch, "E108.21.0.3", {"start": v(285.75, 65.88) * mm, "end": v(285.75, 68.26) * mm});
            skLineSegment(sketch, "E108.21.0.4", {"start": v(273.05, 65.88) * mm, "end": v(279.4, 65.88) * mm, "construction": true});
            skLineSegment(sketch, "E108.direction1", {"start": v(6.35, 65.88) * mm, "end": v(19.05, 65.88) * mm, "construction": true});
            skLineSegment(sketch, "E109", {"start": v(11.4, 63.5) * mm, "end": v(11.4, 65.88) * mm, "construction": true});
            skSolve(sketch);
        }
        {
            var Q0;
            Q0=qSketchRegion(id+"F2",true);
            var Q1;
            Q1=makeQuery(id+"F1.opExtrude","CAP_FACE",FACE,{"disambiguationData":[OSD([sQuery(id+"F0.wireOp",EDGE,"E0.bottom"),sQuery(id+"F0.wireOp",EDGE,"E0.top"),sQuery(id+"F0.wireOp",EDGE,"E0.left"),sQuery(id+"F0.wireOp",EDGE,"E0.right")])],"isStart":true});
            extrude(context, id + "F3", {"entities" : qUnion([Q0]), "operationType" : NewBodyOperationType.REMOVE, "endBound" : BoundingType.UP_TO_SURFACE, "oppositeDirection" : true, "endBoundEntityFace" : qUnion([Q1]), "depth" : 25.4 * mm});
        }
        {
            var Q0;
            Q0=makeQuery(id+"F1.opExtrude","SWEPT_FACE",FACE,{"disambiguationData":[OSD([sQuery(id+"F0.wireOp",EDGE,"E0.left")])]});
            var sketch = newSketch(context, id + "F4", { "sketchPlane" : qUnion([Q0])});
            skLineSegment(sketch, "E110.bottom", {"start": v(-2.38, 3.18) * mm, "end": v(0.8, 3.18) * mm});
            skLineSegment(sketch, "E110.top", {"start": v(-2.38, 0) * mm, "end": v(0.8, 0) * mm});
            skLineSegment(sketch, "E110.left", {"start": v(-2.38, 3.18) * mm, "end": v(-2.38, 0) * mm});
            skLineSegment(sketch, "E110.right", {"start": v(0.8, 3.17) * mm, "end": v(0.8, 0) * mm});
            skLineSegment(sketch, "E111.bottom", {"start": v(-65.88, 0) * mm, "end": v(-69.06, 0) * mm});
            skLineSegment(sketch, "E111.top", {"start": v(-65.88, 3.18) * mm, "end": v(-69.06, 3.18) * mm});
            skLineSegment(sketch, "E111.left", {"start": v(-65.88, 0) * mm, "end": v(-65.88, 3.18) * mm});
            skLineSegment(sketch, "E111.right", {"start": v(-69.06, 0) * mm, "end": v(-69.06, 3.18) * mm});
            skSolve(sketch);
        }
        {
            var Q0;
            Q0 = qSketchRegion(id + "F4", true);
            var Q1;
            Q1=makeQuery(id+"F1.opExtrude","SWEPT_FACE",FACE,{"disambiguationData":[OSD([sQuery(id+"F0.wireOp",EDGE,"E0.right")])]});
            extrude(context, id + "F5", {"entities" : qUnion([Q0]), "operationType" : NewBodyOperationType.ADD, "endBound" : BoundingType.UP_TO_SURFACE, "oppositeDirection" : true, "endBoundEntityFace" : qUnion([Q1]), "depth" : 25.4 * mm});
        }
    });
